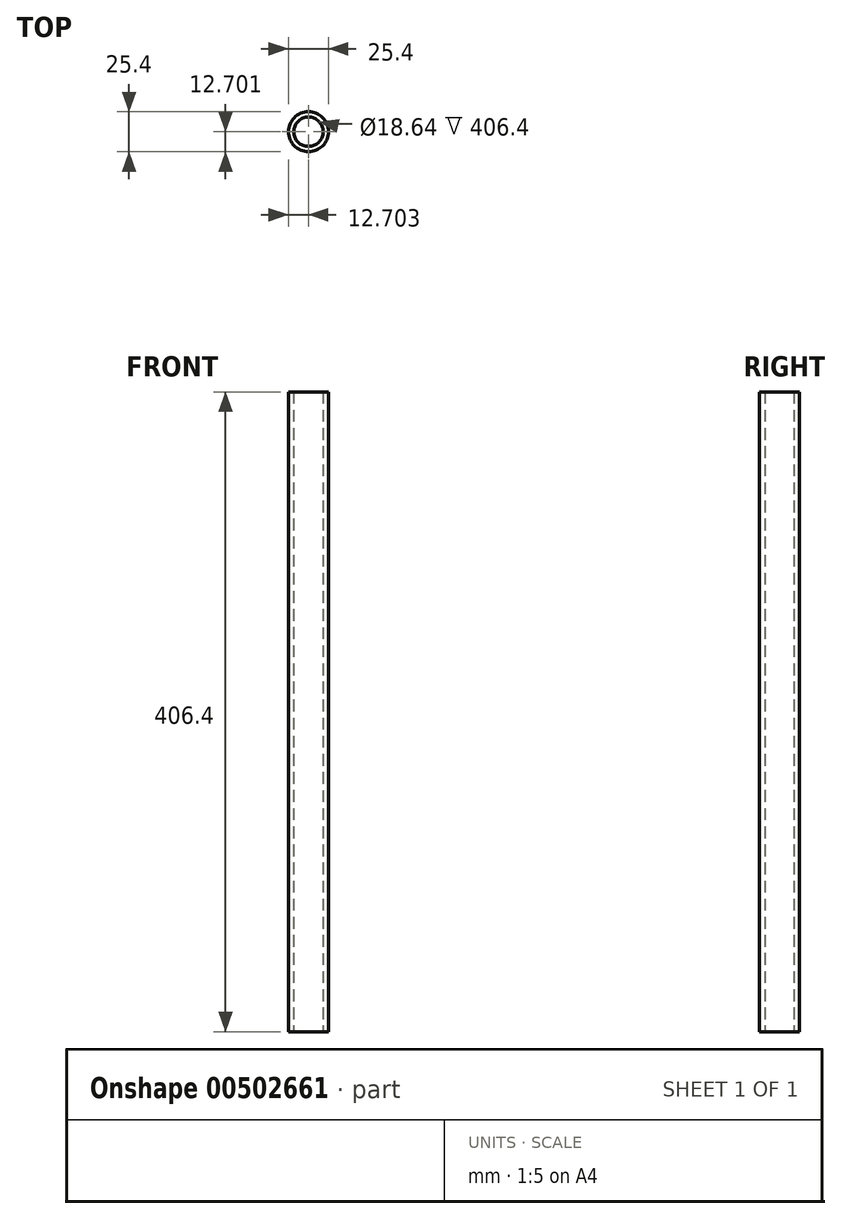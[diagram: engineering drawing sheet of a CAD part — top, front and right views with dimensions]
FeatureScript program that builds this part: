
annotation { "Feature Type Name" : "Feature", "Feature Type Description" : "" }
export const myFeature = defineFeature(function(context is Context, id is Id, definition is map)
    precondition{}
    {
        {
            var Q0;
            Q0=qCreatedBy(makeId("Top.planeOp"),FACE);
            var sketch = newSketch(context, id + "F0", { "sketchPlane" : qUnion([Q0])});
            skCircle(sketch, "E0", {"center": v(47.58, -48.34) * mm, "radius": 12.7 * mm});
            skCircle(sketch, "E1", {"center": v(47.58, -48.34) * mm, "radius": 9.32 * mm});
            skCircle(sketch, "E2", {"center": v(-58.04, -192.54) * mm, "radius": 58.48 * mm});
            skSolve(sketch);
        }
        {
            var Q0;
            Q0=makeQuery(id+"F0.imprint","IMPRINT",FACE,{"disambiguationData":[TD([[makeQuery(id+"F0.imprint","IMPRINT",EDGE,{"derivedFrom":sQuery(id+"F0.wireOp",EDGE,"E0")}),1.0]])]});
            extrude(context, id + "F1", {"entities" : qUnion([Q0]), "depth" : 406.4 * mm});
        }
    });
